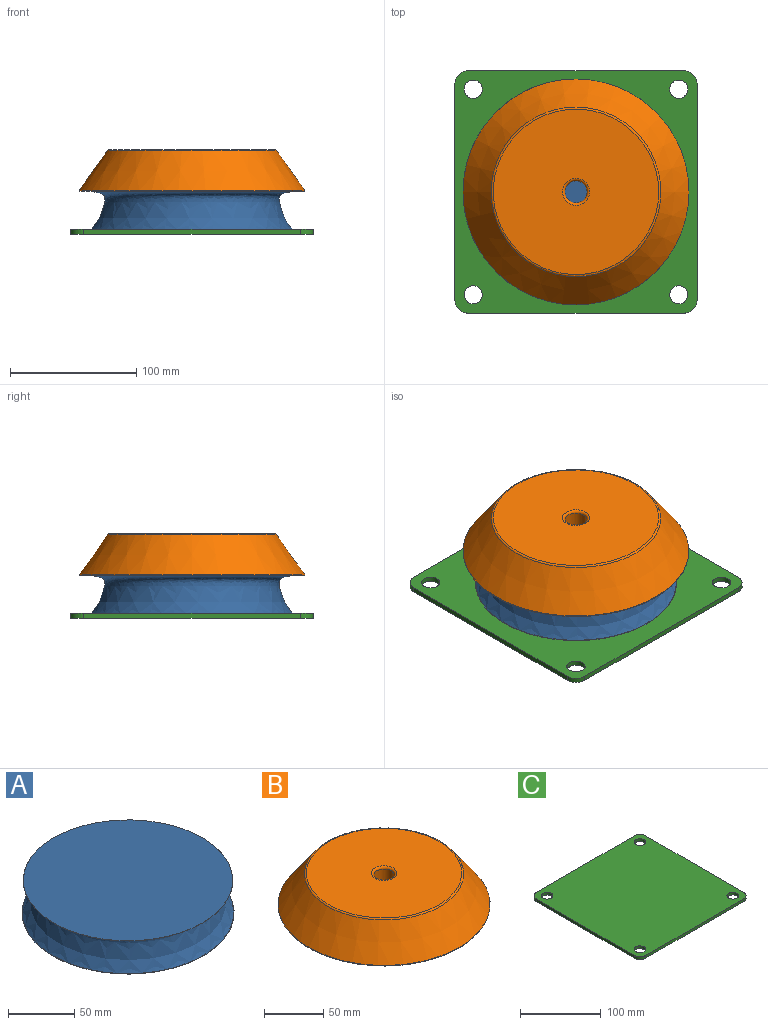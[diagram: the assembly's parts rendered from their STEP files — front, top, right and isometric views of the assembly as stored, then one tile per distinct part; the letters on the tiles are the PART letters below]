
ASSEMBLY  parts=3 mates=2
PART A: 5 faces, bbox 170.8x170.8x30 mm
  f0: revolved ~159.67x159.67mm, area 169.1mm2, adj f1,f3
  f1: revolved ~159.03x159.03mm, area 35869.9mm2, adj f0,f4
  f2: plane 157.64x157.64mm, normal (0,0,1), area 19517.2mm2, adj f4
  f3: plane 159.67x159.67mm, normal (0,0,-1), area 20022.2mm2, adj f0
  f4: torus R=78.82mm, axis (0,0,1), area 149.2mm2, adj f1,f2
PART B: 7 faces, bbox 193.8x193.8x33 mm
  f0: plane 178.06x178.06mm, normal (0,0,-1), area 24662.1mm2, adj f4,f6
  f1: plane 131.12x131.12mm, normal (0,0,1), area 13139.8mm2, adj f3,f5
  f2: cone r=90mm half-angle=35.3deg, axis (0,0,-1), area 18923.7mm2, adj f3,f6
  f3: torus R=65.56mm, axis (0,0,1), area 796.4mm2, adj f1,f2
  f4: cylinder r=8.75mm len=31mm, axis (0,0,1), area 1704.3mm2, adj f0,f5
  f5: torus R=10.75mm, axis (0,0,1), area 187.1mm2, adj f1,f4
  f6: torus R=89.03mm, axis (0,0,1), area 614.4mm2, adj f0,f2
PART C: 14 faces, bbox 192x192x4 mm
  f0: plane 172x4mm, normal (1,0,0), area 688mm2, adj f4,f5,f10,f13
  f1: plane 172x4mm, normal (0,1,0), area 688mm2, adj f4,f5,f10,f11
  f2: plane 172x4mm, normal (-1,0,0), area 688mm2, adj f4,f5,f11,f12
  f3: plane 172x4mm, normal (0,-1,0), area 688mm2, adj f4,f5,f12,f13
  f4: plane 192x192mm, normal (0,0,1), area 36117.6mm2, adj f0,f1,f2,f3,f6,f7,f8,f9
  f5: plane 192x192mm, normal (0,0,-1), area 36117.6mm2, adj f0,f1,f2,f3,f6,f7,f8,f9
  f6: cylinder r=7.25mm len=14.5mm, axis (0,0,1), area 182.2mm2, adj f4,f5
  f7: cylinder r=7.25mm len=14.5mm, axis (0,0,1), area 182.2mm2, adj f4,f5
  f8: cylinder r=7.25mm len=14.5mm, axis (0,0,1), area 182.2mm2, adj f4,f5
  f9: cylinder r=7.25mm len=14.5mm, axis (0,0,1), area 182.2mm2, adj f4,f5
  f10: cylinder r=10mm len=10mm, axis (0,0,1), area 62.8mm2, adj f0,f1,f4,f5
  f11: cylinder r=10mm len=10mm, axis (0,0,-1), area 62.8mm2, adj f1,f2,f4,f5
  f12: cylinder r=10mm len=10mm, axis (0,0,1), area 62.8mm2, adj f2,f3,f4,f5
  f13: cylinder r=10mm len=10mm, axis (0,0,-1), area 62.8mm2, adj f0,f3,f4,f5
PLACE A t=(166.13,-4.51,14.06)mm
PLACE B t=(166.13,-4.51,48.06)mm
PLACE C rot(axis=(0,0,-1),90deg) t=(166.13,-4.51,14.1)mm
MATE planar A.f4 <-> B.f4  axis (0,0,1) through (166.13,-4.51,48.06)mm
MATE planar C.f4 <-> A.f4  axis (0,0,1) through (166.13,-4.51,18.1)mm
